# Revit family: Gitterrinne GRM - GRM 55 150 G
name_source: partatom
category: Generic Models
revit_build: Autodesk Revit 2017 (Build: 20190508_0315(x64)
units: mm (PartAtom-declared; Revit-internal decimal feet)

## family parameters
Always vertical = Yes
Can host rebar = No
Cut with Voids When Loaded = No
Part Type = Normal
Room Calculation Point = No
Round Connector Dimension = Use Diameter
Shared = No
Work Plane-Based = No

## types (4) — shared parameters
Length = 3000 mm  [stored 9.84252 ft]
Manufacturer = OBO Bettermann
URL = http://www.obo-bettermann.com
Width = 150 mm
Width 1 = 75 mm

## per-type parameters (varying)
| type | Article Type | GTIN | Manufacturer Art.No. | Material |
| GRM 55 150 G | GRM 55 150 G | 4012196078974 | 6001444 | Electrogalvanised |
| GRM 55 150 A4 | GRM 55 150 A4 | 4012195166023 | 6001090 | Stainless steel, A4 |
| GRM 55 150 A2 | GRM 55 150 A42 | 4012196101351 | 6001074 | Stainless steel, A2 |
| GRM 55 150 FT | GRM 55 150 FT | 4012196078912 | 6001418 | Hot-dip galvanised |

note: [stored X ft] marks values corroborated as IEEE doubles in the binary element streams (Revit-internal decimal feet)

## geometry (parser evidence)
native form markers: Sweep x2
no freeform markers — native parametric forms only
